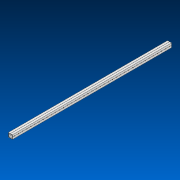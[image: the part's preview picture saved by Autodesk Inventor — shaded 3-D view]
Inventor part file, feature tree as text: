
AUTODESK INVENTOR PART (.ipt)
format: ipt  version: 2022.2 (Build 262287000, 287)  size: 817,664 bytes
history: native  units: in
note: dims shown in document units (in); Inventor stores cm internally (conversion verified against a paired STEP export)
features: other x39, extrude x1, pattern_linear x1, sketch x1, pattern_circular x1
ambient origin geometry x8: Origin, YZ Plane, XZ Plane, XY Plane, X Axis, Y Axis, Z Axis, Center Point
bodies: Solid1 (feature_tree)
feature tree (43):
  extrude  "Extrusion1"  Depth=1.0in
  other  "Work Axis1"
  pattern_linear  "Rectangular Pattern1"  Spacing1=0.0in  [1 undecoded]
  sketch  "Sketch1"  dims[d0=1.0in d1=20.0in d2=0.0in d3=15.3543in d5=1.0in]
  other  "Work Axis2"
  other  "Work Axis3"
  other  "Work Axis4"
  other  "Work Axis5"
  other  "Work Axis6"
  other  "Work Axis7"
  other  "Work Axis8"
  other  "Work Axis9"
  other  "Work Axis10"
  other  "Work Axis11"
  other  "Work Axis12"
  other  "Work Axis13"
  other  "Work Axis14"
  other  "Work Axis15"
  other  "Work Axis16"
  other  "Work Axis17"
  other  "Work Axis18"
  other  "Work Axis19"
  other  "Work Axis20"
  other  "Work Axis21"
  other  "Work Axis22"
  other  "Work Axis23"
  other  "Work Axis24"
  other  "Work Axis25"
  other  "Work Axis26"
  other  "Work Axis27"
  other  "Work Axis28"
  other  "Work Axis29"
  other  "Work Axis30"
  other  "Work Axis31"
  other  "Work Axis32"
  other  "Work Axis33"
  other  "Work Axis34"
  other  "Work Axis35"
  other  "Work Axis36"
  other  "Work Axis37"
  other  "Work Axis38"
  other  "Work Axis39"
  pattern_circular  "CirPattern2"
note: 1 required parameter value undecoded (feature->parameter linkage not recoverable at this tier; creation-order binding heuristic only, values carry confidence <= 0.55)
